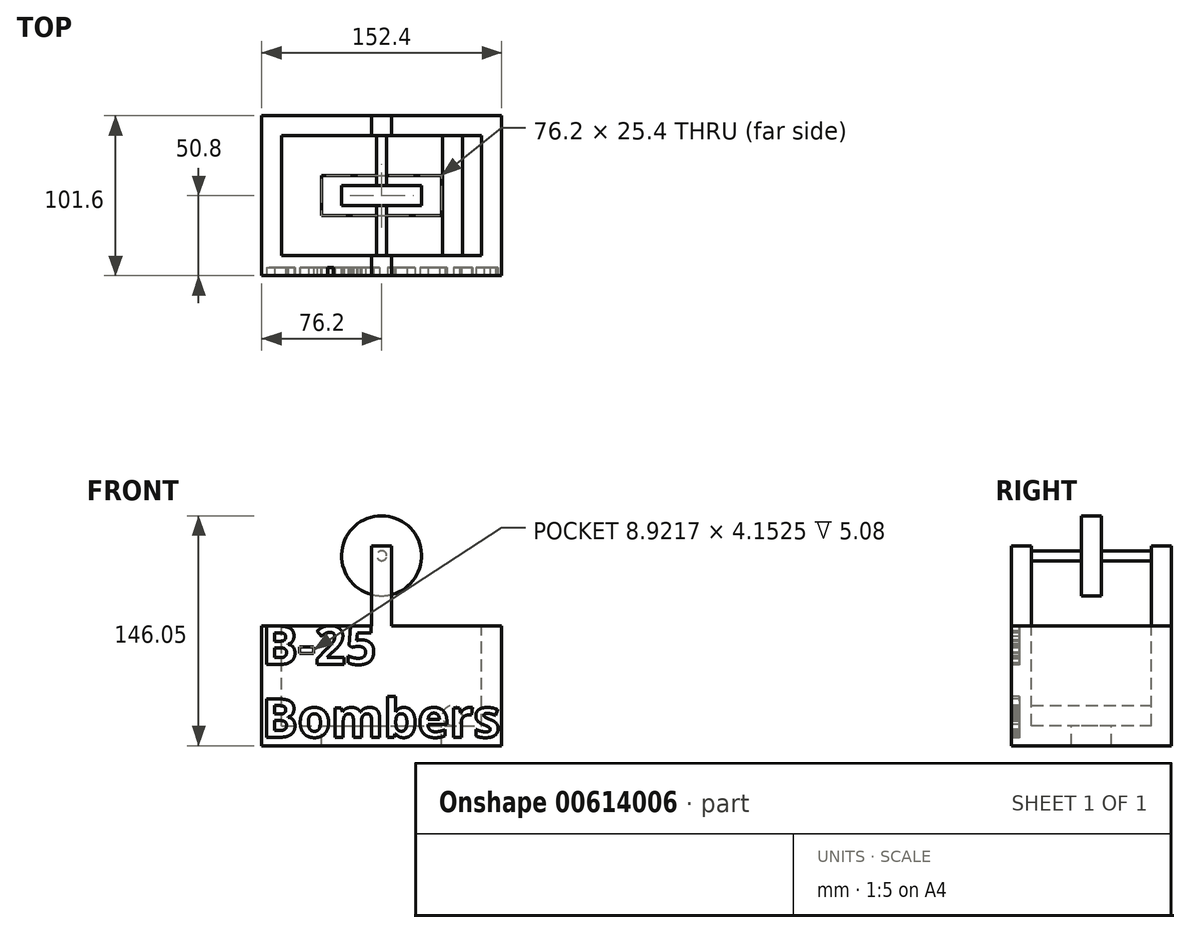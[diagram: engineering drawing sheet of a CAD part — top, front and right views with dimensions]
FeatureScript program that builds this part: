
annotation { "Feature Type Name" : "Feature", "Feature Type Description" : "" }
export const myFeature = defineFeature(function(context is Context, id is Id, definition is map)
    precondition{}
    {
        {
            var Q0;
            Q0=qCreatedBy(makeId("Front.planeOp"),FACE);
            var sketch = newSketch(context, id + "F0", { "sketchPlane" : qUnion([Q0])});
            skLineSegment(sketch, "E0.bottom", {"start": v(0, 0) * mm, "end": v(152.4, 0) * mm});
            skLineSegment(sketch, "E0.top", {"start": v(0, 76.2) * mm, "end": v(152.4, 76.2) * mm});
            skLineSegment(sketch, "E0.left", {"start": v(0, 0) * mm, "end": v(0, 76.2) * mm});
            skLineSegment(sketch, "E0.right", {"start": v(152.4, 0) * mm, "end": v(152.4, 76.2) * mm});
            skSolve(sketch);
        }
        {
            var Q0;
            Q0=makeQuery(id+"F0.imprint","IMPRINT",FACE,{"disambiguationData":[TD([[makeQuery(id+"F0.imprint","IMPRINT",EDGE,{"derivedFrom":sQuery(id+"F0.wireOp",EDGE,"E0.bottom")}),1.0]])]});
            extrude(context, id + "F1", {"entities" : qUnion([Q0]), "oppositeDirection" : true, "depth" : 101.6 * mm, "offsetDistance" : 25.4 * mm});
        }
        {
            var Q0;
            Q0=makeQuery(id+"F1.opExtrude","SWEPT_FACE",FACE,{"disambiguationData":[OSD([sQuery(id+"F0.wireOp",EDGE,"E0.top")])]});
            var sketch = newSketch(context, id + "F2", { "sketchPlane" : qUnion([Q0])});
            skLineSegment(sketch, "E1.bottom", {"start": v(12.7, 88.9) * mm, "end": v(139.7, 88.9) * mm});
            skLineSegment(sketch, "E1.top", {"start": v(12.7, 12.7) * mm, "end": v(139.7, 12.7) * mm});
            skLineSegment(sketch, "E1.left", {"start": v(12.7, 88.9) * mm, "end": v(12.7, 12.7) * mm});
            skLineSegment(sketch, "E1.right", {"start": v(139.7, 88.9) * mm, "end": v(139.7, 12.7) * mm});
            skSolve(sketch);
        }
        {
            var Q0;
            Q0=makeQuery(id+"F2.imprint","IMPRINT",FACE,{"disambiguationData":[TD([[makeQuery(id+"F2.imprint","IMPRINT",EDGE,{"derivedFrom":sQuery(id+"F2.wireOp",EDGE,"E1.bottom")}),-1.0]])]});
            extrude(context, id + "F3", {"entities" : qUnion([Q0]), "operationType" : NewBodyOperationType.REMOVE, "oppositeDirection" : true, "depth" : 63.5 * mm, "offsetDistance" : 25.4 * mm});
        }
        {
            var Q0;
            Q0=makeQuery(id+"F3.boolean.opBoolean","COPY",FACE,{"derivedFrom":makeQuery(id+"F3.opExtrude","CAP_FACE",FACE,{"disambiguationData":[OSD([sQuery(id+"F2.wireOp",EDGE,"E1.bottom"),sQuery(id+"F2.wireOp",EDGE,"E1.top"),sQuery(id+"F2.wireOp",EDGE,"E1.left"),sQuery(id+"F2.wireOp",EDGE,"E1.right")])],"isStart":false})});
            var sketch = newSketch(context, id + "F4", { "sketchPlane" : qUnion([Q0])});
            skLineSegment(sketch, "E2.bottom", {"start": v(38.1, 63.5) * mm, "end": v(114.3, 63.5) * mm});
            skLineSegment(sketch, "E2.top", {"start": v(38.1, 38.1) * mm, "end": v(114.3, 38.1) * mm});
            skLineSegment(sketch, "E2.left", {"start": v(38.1, 63.5) * mm, "end": v(38.1, 38.1) * mm});
            skLineSegment(sketch, "E2.right", {"start": v(114.3, 63.5) * mm, "end": v(114.3, 38.1) * mm});
            skSolve(sketch);
        }
        {
            var Q0;
            Q0=makeQuery(id+"F4.imprint","IMPRINT",FACE,{"disambiguationData":[TD([[makeQuery(id+"F4.imprint","IMPRINT",EDGE,{"derivedFrom":sQuery(id+"F4.wireOp",EDGE,"E2.bottom")}),-1.0]])]});
            extrude(context, id + "F5", {"entities" : qUnion([Q0]), "operationType" : NewBodyOperationType.REMOVE, "oppositeDirection" : true, "depth" : 12.7 * mm, "offsetDistance" : 25.4 * mm});
        }
        {
            var Q0;
            Q0=makeQuery(id+"F1.opExtrude","SWEPT_FACE",FACE,{"disambiguationData":[OSD([sQuery(id+"F0.wireOp",EDGE,"E0.top")])]});
            var sketch = newSketch(context, id + "F6", { "sketchPlane" : qUnion([Q0])});
            skLineSegment(sketch, "E3.bottom", {"start": v(69.85, 101.6) * mm, "end": v(82.55, 101.6) * mm});
            skLineSegment(sketch, "E3.top", {"start": v(69.85, 88.9) * mm, "end": v(82.55, 88.9) * mm});
            skLineSegment(sketch, "E3.left", {"start": v(69.85, 101.6) * mm, "end": v(69.85, 88.9) * mm});
            skLineSegment(sketch, "E3.right", {"start": v(82.55, 101.6) * mm, "end": v(82.55, 88.9) * mm});
            skSolve(sketch);
        }
        {
            var Q0;
            Q0=makeQuery(id+"F6.imprint","IMPRINT",FACE,{"disambiguationData":[TD([[makeQuery(id+"F6.imprint","IMPRINT",EDGE,{"derivedFrom":sQuery(id+"F6.wireOp",EDGE,"E3.bottom")}),-1.0]])]});
            extrude(context, id + "F7", {"entities" : qUnion([Q0]), "operationType" : NewBodyOperationType.ADD, "depth" : 50.8 * mm, "offsetDistance" : 25.4 * mm});
        }
        {
            var Q0;
            Q0=makeQuery(id+"F1.opExtrude","SWEPT_FACE",FACE,{"disambiguationData":[OSD([sQuery(id+"F0.wireOp",EDGE,"E0.top")])]});
            var sketch = newSketch(context, id + "F8", { "sketchPlane" : qUnion([Q0])});
            skLineSegment(sketch, "E4.bottom", {"start": v(69.85, 12.7) * mm, "end": v(82.55, 12.7) * mm});
            skLineSegment(sketch, "E4.top", {"start": v(69.85, 0) * mm, "end": v(82.55, 0) * mm});
            skLineSegment(sketch, "E4.left", {"start": v(69.85, 12.7) * mm, "end": v(69.85, 0) * mm});
            skLineSegment(sketch, "E4.right", {"start": v(82.55, 12.7) * mm, "end": v(82.55, 0) * mm});
            skSolve(sketch);
        }
        {
            var Q0;
            Q0=makeQuery(id+"F8.imprint","IMPRINT",FACE,{"disambiguationData":[TD([[makeQuery(id+"F8.imprint","IMPRINT",EDGE,{"derivedFrom":sQuery(id+"F8.wireOp",EDGE,"E4.bottom")}),-1.0]])]});
            extrude(context, id + "F9", {"entities" : qUnion([Q0]), "operationType" : NewBodyOperationType.ADD, "depth" : 50.8 * mm, "offsetDistance" : 25.4 * mm});
        }
        {
            var Q0;
            Q0=makeQuery(id+"F9.boolean.opBoolean","MERGE",FACE,{"derivedFrom":[makeQuery(id+"F1.opExtrude","CAP_FACE",FACE,{"disambiguationData":[OSD([sQuery(id+"F0.wireOp",EDGE,"E0.bottom"),sQuery(id+"F0.wireOp",EDGE,"E0.top"),sQuery(id+"F0.wireOp",EDGE,"E0.left"),sQuery(id+"F0.wireOp",EDGE,"E0.right")])],"isStart":true}),makeQuery(id+"F9.opExtrude","SWEPT_FACE",FACE,{"disambiguationData":[OSD([sQuery(id+"F8.wireOp",EDGE,"E4.top")])]})]});
            var sketch = newSketch(context, id + "F10", { "sketchPlane" : qUnion([Q0])});
            skCircle(sketch, "E5", {"center": v(76.2, 120.65) * mm, "radius": 3.18 * mm});
            skSolve(sketch);
        }
        {
            var Q0;
            Q0=makeQuery(id+"F10.imprint","IMPRINT",FACE,{"disambiguationData":[TD([[makeQuery(id+"F10.imprint","IMPRINT",EDGE,{"derivedFrom":sQuery(id+"F10.wireOp",EDGE,"E5")}),1.0]])]});
            extrude(context, id + "F11", {"entities" : qUnion([Q0]), "operationType" : NewBodyOperationType.ADD, "oppositeDirection" : true, "depth" : 101.6 * mm, "offsetDistance" : 25.4 * mm});
        }
        {
            var Q0;
            Q0=qCreatedBy(makeId("Front.planeOp"),FACE);
            cPlane(context, id + "F12", {"entities" : qUnion([Q0]), "cplaneType" : CPlaneType.OFFSET, "offset" : 50.8 * mm, "oppositeDirection" : true, "width" : 152.4 * mm, "height" : 152.4 * mm});
        }
        {
            var Q0;
            Q0=qCreatedBy(id+"F12.planeOp",FACE);
            var sketch = newSketch(context, id + "F13", { "sketchPlane" : qUnion([Q0])});
            skCircle(sketch, "E6", {"center": v(76.1, 120.65) * mm, "radius": 25.4 * mm});
            skSolve(sketch);
        }
        {
            var Q0;
            Q0=makeQuery(id+"F13.imprint","IMPRINT",FACE,{"disambiguationData":[TD([[makeQuery(id+"F13.imprint","IMPRINT",EDGE,{"derivedFrom":sQuery(id+"F13.wireOp",EDGE,"E6")}),1.0]])]});
            extrude(context, id + "F14", {"entities" : qUnion([Q0]), "operationType" : NewBodyOperationType.ADD, "endBound" : BoundingType.SYMMETRIC, "depth" : 12.7 * mm, "offsetDistance" : 25.4 * mm});
        }
        {
            var Q0;
            Q0=makeQuery(id+"F7.boolean.opBoolean","MERGE",FACE,{"derivedFrom":[makeQuery(id+"F3.boolean.opBoolean","COPY",FACE,{"derivedFrom":makeQuery(id+"F3.opExtrude","SWEPT_FACE",FACE,{"disambiguationData":[OSD([sQuery(id+"F2.wireOp",EDGE,"E1.bottom")])]})}),makeQuery(id+"F7.opExtrude","SWEPT_FACE",FACE,{"disambiguationData":[OSD([sQuery(id+"F6.wireOp",EDGE,"E3.top")])]})]});
            var sketch = newSketch(context, id + "F15", { "sketchPlane" : qUnion([Q0])});
            skCircle(sketch, "E7", {"center": v(121.06, 19.14) * mm, "radius": 6.35 * mm});
            skSolve(sketch);
        }
        {
            var Q0;
            Q0=makeQuery(id+"F15.imprint","IMPRINT",FACE,{"disambiguationData":[TD([[makeQuery(id+"F15.imprint","IMPRINT",EDGE,{"derivedFrom":sQuery(id+"F15.wireOp",EDGE,"E7")}),1.0]])]});
            extrude(context, id + "F16", {"entities" : qUnion([Q0]), "operationType" : NewBodyOperationType.ADD, "depth" : 76.2 * mm, "offsetDistance" : 25.4 * mm});
        }
        {
            var Q0;
            Q0=makeQuery(id+"F9.boolean.opBoolean","MERGE",FACE,{"derivedFrom":[makeQuery(id+"F1.opExtrude","CAP_FACE",FACE,{"disambiguationData":[OSD([sQuery(id+"F0.wireOp",EDGE,"E0.bottom"),sQuery(id+"F0.wireOp",EDGE,"E0.top"),sQuery(id+"F0.wireOp",EDGE,"E0.left"),sQuery(id+"F0.wireOp",EDGE,"E0.right")])],"isStart":true}),makeQuery(id+"F9.opExtrude","SWEPT_FACE",FACE,{"disambiguationData":[OSD([sQuery(id+"F8.wireOp",EDGE,"E4.top")])]})]});
            var sketch = newSketch(context, id + "F17", { "sketchPlane" : qUnion([Q0])});
            skText(sketch, "E8", { "text": "B-25\nBombers", "fontName": "OpenSans-Bold.ttf"});
            const initialGuessF17  = {"E8": [0, 0.0517, 1, 0, 0.0245]};
            skSetInitialGuess(sketch, initialGuessF17);
            skSolve(sketch);
        }
        {
            var Q0;
            Q0 = qSketchRegion(id + "F17", true);
            extrude(context, id + "F18", {"entities" : qUnion([Q0]), "operationType" : NewBodyOperationType.REMOVE, "oppositeDirection" : true, "depth" : 5.08 * mm, "offsetDistance" : 25.4 * mm});
        }
    });
